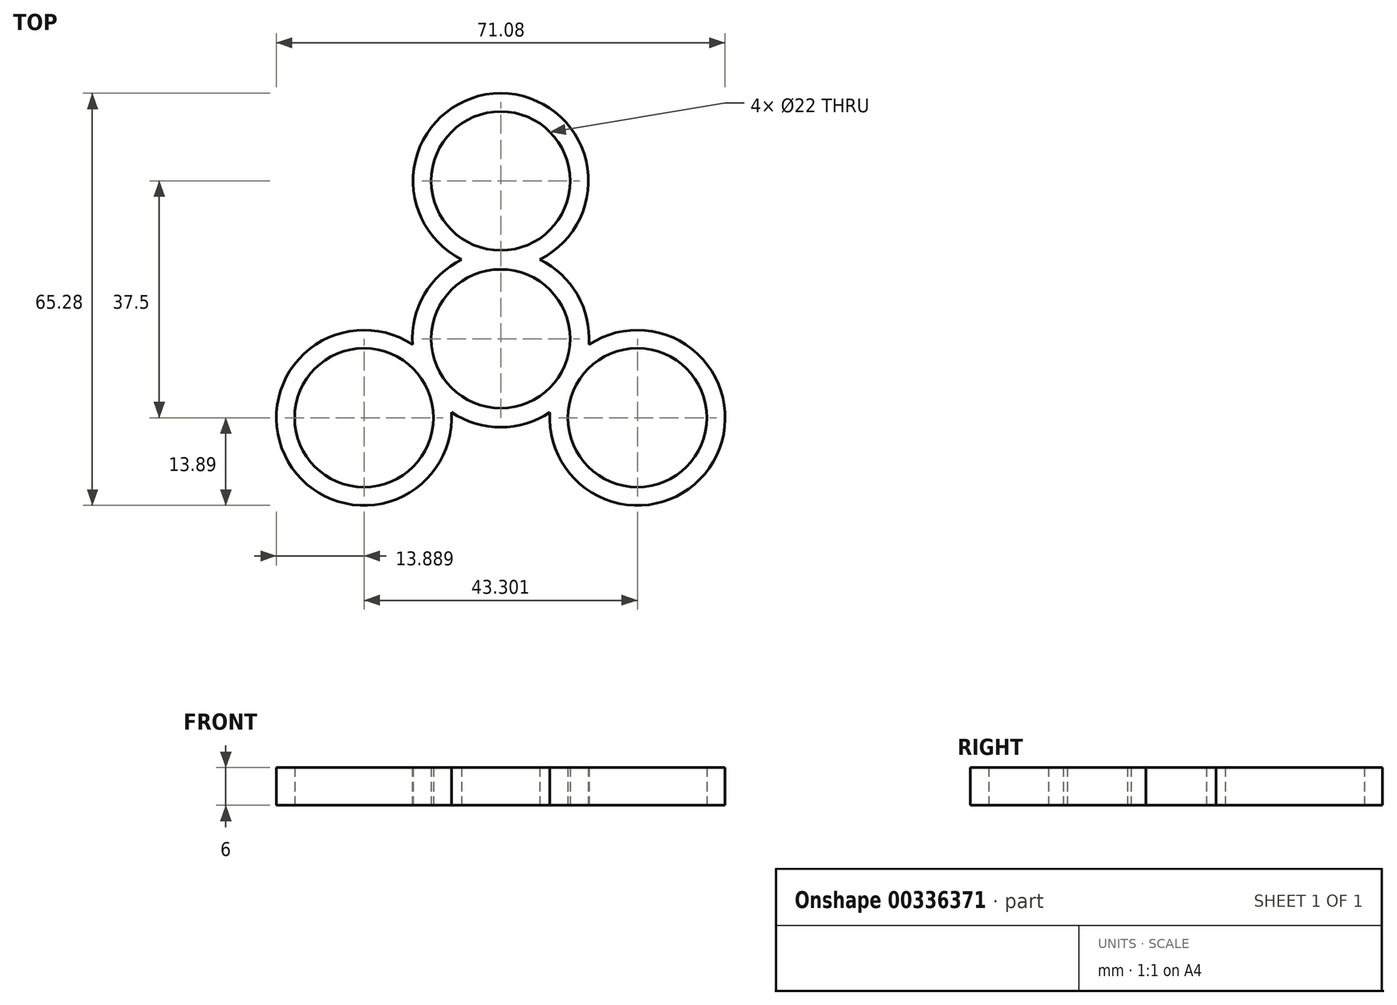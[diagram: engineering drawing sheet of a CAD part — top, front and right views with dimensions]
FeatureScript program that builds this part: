
annotation { "Feature Type Name" : "Feature", "Feature Type Description" : "" }
export const myFeature = defineFeature(function(context is Context, id is Id, definition is map)
    precondition{}
    {
        {
            var Q0;
            Q0=qCreatedBy(makeId("Top.planeOp"),FACE);
            var sketch = newSketch(context, id + "F0", { "sketchPlane" : qUnion([Q0])});
            skArc(sketch, "E0", {"start": v(9.53, 5.5) * mm, "mid": v(0, 11) * mm, "end": v(-9.53, 5.5) * mm});
            skCircle(sketch, "E1", {"center": v(0, 25) * mm, "radius": 11 * mm});
            skArc(sketch, "E2", {"start": v(-6.18, 12.56) * mm, "mid": v(-9.57, 10.22) * mm, "end": v(-12.12, 7) * mm});
            skArc(sketch, "E3", {"start": v(6.18, 12.56) * mm, "mid": v(0, 38.89) * mm, "end": v(-6.18, 12.56) * mm});
            skArc(sketch, "E4.trimOffspring", {"start": v(12.12, 7) * mm, "mid": v(9.57, 10.22) * mm, "end": v(6.18, 12.56) * mm});
            skArc(sketch, "E5.MirrorCS", {"start": v(-7.79, -11.63) * mm, "mid": v(-33.68, -19.44) * mm, "end": v(-13.97, -0.93) * mm});
            skArc(sketch, "E6.MirrorCS", {"start": v(-13.97, -0.93) * mm, "mid": v(-13.64, 3.17) * mm, "end": v(-12.12, 7) * mm});
            skArc(sketch, "E7.MirrorCS", {"start": v(0, -11) * mm, "mid": v(-9.53, -5.5) * mm, "end": v(-9.53, 5.5) * mm});
            skArc(sketch, "E8.MirrorCS", {"start": v(0, -14) * mm, "mid": v(-4.07, -13.4) * mm, "end": v(-7.79, -11.63) * mm});
            skCircle(sketch, "E9.MirrorC", {"center": v(-21.65, -12.5) * mm, "radius": 11 * mm});
            skArc(sketch, "E10.MirrorCS", {"start": v(9.53, 5.5) * mm, "mid": v(9.53, -5.5) * mm, "end": v(0, -11) * mm});
            skArc(sketch, "E11.MirrorCS", {"start": v(12.12, 7) * mm, "mid": v(13.64, 3.17) * mm, "end": v(13.97, -0.93) * mm});
            skArc(sketch, "E12.MirrorCS", {"start": v(13.97, -0.93) * mm, "mid": v(33.68, -19.44) * mm, "end": v(7.79, -11.63) * mm});
            skArc(sketch, "E13.MirrorCS", {"start": v(7.79, -11.63) * mm, "mid": v(4.07, -13.4) * mm, "end": v(0, -14) * mm});
            skCircle(sketch, "E14.MirrorC", {"center": v(21.65, -12.5) * mm, "radius": 11 * mm});
            skSolve(sketch);
        }
        {
            var Q0;
            Q0=makeQuery(id+"F0.imprint","IMPRINT",FACE,{"disambiguationData":[TD([[makeQuery(id+"F0.imprint","IMPRINT",EDGE,{"derivedFrom":sQuery(id+"F0.wireOp",EDGE,"E0")}),-1.0]])]});
            extrude(context, id + "F1", {"entities" : qUnion([Q0]), "depth" : 6 * mm, "offsetDistance" : 25 * mm});
        }
    });
